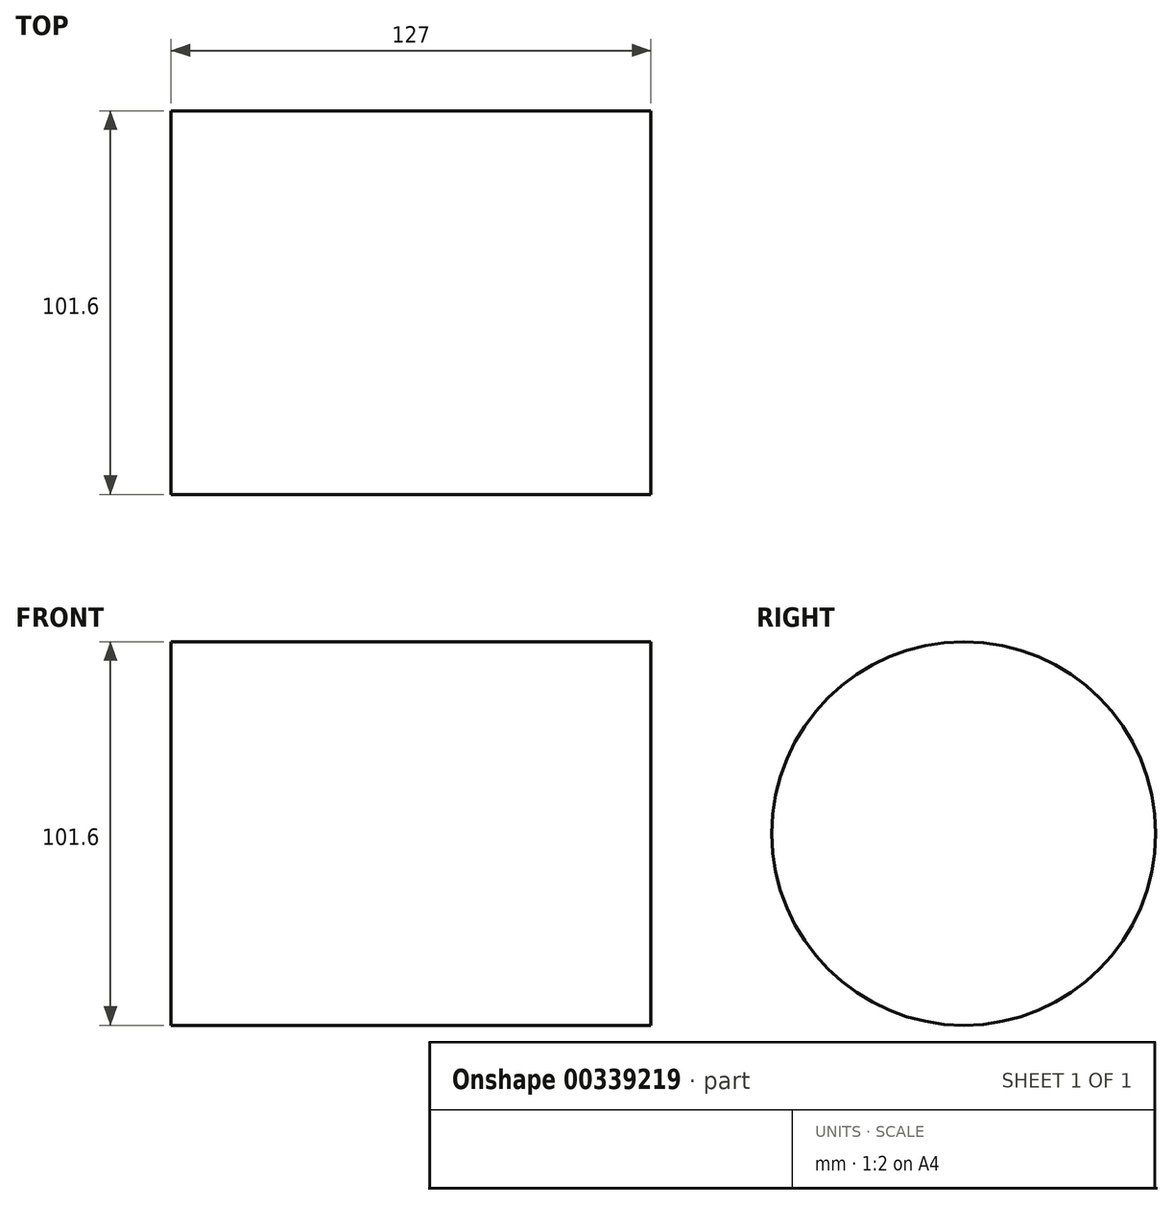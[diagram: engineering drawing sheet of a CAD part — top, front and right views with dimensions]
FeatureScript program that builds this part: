
annotation { "Feature Type Name" : "Feature", "Feature Type Description" : "" }
export const myFeature = defineFeature(function(context is Context, id is Id, definition is map)
    precondition{}
    {
        {
            var Q0;
            Q0=qCreatedBy(makeId("Right.planeOp"),FACE);
            var sketch = newSketch(context, id + "F0", { "sketchPlane" : qUnion([Q0])});
            skCircle(sketch, "E0", {"center": v(0, 0) * mm, "radius": 50.8 * mm});
            skSolve(sketch);
        }
        {
            var Q0;
            Q0=makeQuery(id+"F0.imprint","IMPRINT",FACE,{"disambiguationData":[TD([[makeQuery(id+"F0.imprint","IMPRINT",EDGE,{"derivedFrom":sQuery(id+"F0.wireOp",EDGE,"E0")}),1.0]])]});
            extrude(context, id + "F1", {"entities" : qUnion([Q0]), "depth" : 127 * mm});
        }
    });
